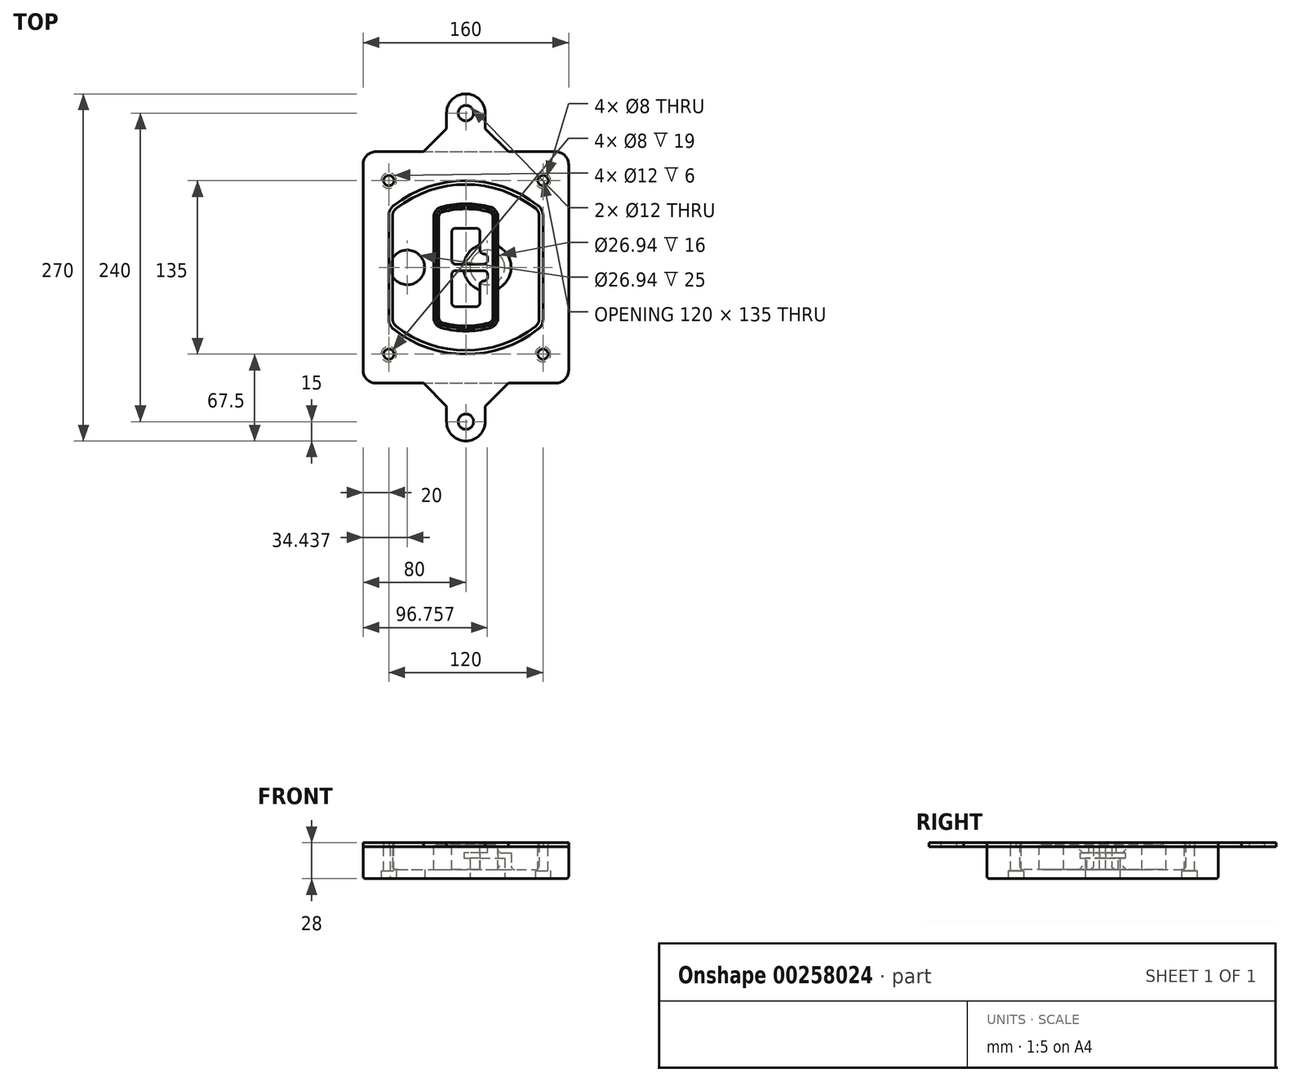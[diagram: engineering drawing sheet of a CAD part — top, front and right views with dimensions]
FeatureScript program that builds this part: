
annotation { "Feature Type Name" : "Feature", "Feature Type Description" : "" }
export const myFeature = defineFeature(function(context is Context, id is Id, definition is map)
    precondition{}
    {
        {
            var Q0;
            Q0=qCreatedBy(makeId("Top.planeOp"),FACE);
            var sketch = newSketch(context, id + "F0", { "sketchPlane" : qUnion([Q0])});
            skPoint(sketch, "E0.rect.middle", {"position": v(0, 0) * mm});
            skLineSegment(sketch, "E1.bottom", {"start": v(-70, -90) * mm, "end": v(70, -90) * mm});
            skLineSegment(sketch, "E1.top", {"start": v(-70, 90) * mm, "end": v(70, 90) * mm});
            skLineSegment(sketch, "E1.left", {"start": v(-80, -80) * mm, "end": v(-80, 80) * mm});
            skLineSegment(sketch, "E1.right", {"start": v(80, -80) * mm, "end": v(80, 80) * mm});
            skLineSegment(sketch, "E2", {"start": v(-80, 90) * mm, "end": v(80, -90) * mm, "construction": true});
            skLineSegment(sketch, "E3", {"start": v(80, 90) * mm, "end": v(-80, -90) * mm, "construction": true});
            skCircle(sketch, "E4", {"center": v(-60, 67.5) * mm, "radius": 4 * mm});
            skCircle(sketch, "E5", {"center": v(60, 67.5) * mm, "radius": 4 * mm});
            skCircle(sketch, "E6", {"center": v(60, -67.5) * mm, "radius": 4 * mm});
            skCircle(sketch, "E7", {"center": v(-60, -67.5) * mm, "radius": 4 * mm});
            skLineSegment(sketch, "E8", {"start": v(-60, 67.5) * mm, "end": v(60, 67.5) * mm, "construction": true});
            skLineSegment(sketch, "E9", {"start": v(60, 67.5) * mm, "end": v(60, -67.5) * mm, "construction": true});
            skLineSegment(sketch, "E10", {"start": v(60, -67.5) * mm, "end": v(-60, -67.5) * mm, "construction": true});
            skLineSegment(sketch, "E11", {"start": v(-60, -67.5) * mm, "end": v(-60, 67.5) * mm, "construction": true});
            skLineSegment(sketch, "E12", {"start": v(-60, 40.3) * mm, "end": v(-60, -40.3) * mm});
            skLineSegment(sketch, "E13", {"start": v(60, 40.3) * mm, "end": v(60, -40.3) * mm});
            skArc(sketch, "E14", {"start": v(56.15, 48.18) * mm, "mid": v(0, 67.5) * mm, "end": v(-56.15, 48.18) * mm});
            skArc(sketch, "E15", {"start": v(-56.15, -48.18) * mm, "mid": v(0, -67.5) * mm, "end": v(56.15, -48.18) * mm});
            skLineSegment(sketch, "E16", {"start": v(-60, 0) * mm, "end": v(60, 0) * mm, "construction": true});
            skPoint(sketch, "E17.visualSharp", {"position": v(-60, -45) * mm});
            skArc(sketch, "E17.filletArc", {"start": v(-60, -40.3) * mm, "mid": v(-58.99, -44.68) * mm, "end": v(-56.15, -48.18) * mm});
            skPoint(sketch, "E18.visualSharp", {"position": v(-60, 45) * mm});
            skArc(sketch, "E18.filletArc", {"start": v(-56.15, 48.18) * mm, "mid": v(-58.99, 44.68) * mm, "end": v(-60, 40.3) * mm});
            skPoint(sketch, "E19.visualSharp", {"position": v(60, 45) * mm});
            skArc(sketch, "E19.filletArc", {"start": v(60, 40.3) * mm, "mid": v(58.99, 44.68) * mm, "end": v(56.15, 48.18) * mm});
            skPoint(sketch, "E20.visualSharp", {"position": v(60, -45) * mm});
            skArc(sketch, "E20.filletArc", {"start": v(56.15, -48.18) * mm, "mid": v(58.99, -44.68) * mm, "end": v(60, -40.3) * mm});
            skPoint(sketch, "E21.visualSharp", {"position": v(-80, 90) * mm});
            skArc(sketch, "E21.filletArc", {"start": v(-70, 90) * mm, "mid": v(-77.07, 87.07) * mm, "end": v(-80, 80) * mm});
            skPoint(sketch, "E22.visualSharp", {"position": v(80, 90) * mm});
            skArc(sketch, "E22.filletArc", {"start": v(80, 80) * mm, "mid": v(77.07, 87.07) * mm, "end": v(70, 90) * mm});
            skPoint(sketch, "E23.visualSharp", {"position": v(80, -90) * mm});
            skArc(sketch, "E23.filletArc", {"start": v(70, -90) * mm, "mid": v(77.07, -87.07) * mm, "end": v(80, -80) * mm});
            skPoint(sketch, "E24.visualSharp", {"position": v(-80, -90) * mm});
            skArc(sketch, "E24.filletArc", {"start": v(-80, -80) * mm, "mid": v(-77.07, -87.07) * mm, "end": v(-70, -90) * mm});
            skArc(sketch, "E25.0", {"start": v(57, 40.3) * mm, "mid": v(56.3, 43.36) * mm, "end": v(54.3, 45.81) * mm});
            skLineSegment(sketch, "E25.1", {"start": v(57, 40.3) * mm, "end": v(57, -40.3) * mm});
            skArc(sketch, "E25.2", {"start": v(54.3, -45.81) * mm, "mid": v(56.3, -43.36) * mm, "end": v(57, -40.3) * mm});
            skArc(sketch, "E25.3", {"start": v(-54.3, -45.81) * mm, "mid": v(0, -64.5) * mm, "end": v(54.3, -45.81) * mm});
            skArc(sketch, "E25.4", {"start": v(-57, -40.3) * mm, "mid": v(-56.3, -43.36) * mm, "end": v(-54.3, -45.81) * mm});
            skArc(sketch, "E25.5", {"start": v(54.3, 45.81) * mm, "mid": v(0, 64.5) * mm, "end": v(-54.3, 45.81) * mm});
            skLineSegment(sketch, "E25.6", {"start": v(-57, 40.3) * mm, "end": v(-57, -40.3) * mm});
            skArc(sketch, "E25.7", {"start": v(-54.3, 45.81) * mm, "mid": v(-56.3, 43.36) * mm, "end": v(-57, 40.3) * mm});
            skArc(sketch, "E26.0", {"start": v(-58.62, 51.33) * mm, "mid": v(-62.58, 46.43) * mm, "end": v(-64, 40.3) * mm});
            skArc(sketch, "E26.1", {"start": v(58.62, 51.33) * mm, "mid": v(0, 71.5) * mm, "end": v(-58.62, 51.33) * mm});
            skArc(sketch, "E26.2", {"start": v(64, 40.3) * mm, "mid": v(62.58, 46.43) * mm, "end": v(58.62, 51.33) * mm});
            skLineSegment(sketch, "E26.3", {"start": v(64, 40.3) * mm, "end": v(64, -40.3) * mm});
            skArc(sketch, "E26.4", {"start": v(58.62, -51.33) * mm, "mid": v(62.58, -46.43) * mm, "end": v(64, -40.3) * mm});
            skLineSegment(sketch, "E26.5", {"start": v(-64, 40.3) * mm, "end": v(-64, -40.3) * mm});
            skArc(sketch, "E26.6", {"start": v(-58.62, -51.33) * mm, "mid": v(0, -71.5) * mm, "end": v(58.62, -51.33) * mm});
            skArc(sketch, "E26.7", {"start": v(-64, -40.3) * mm, "mid": v(-62.58, -46.43) * mm, "end": v(-58.62, -51.33) * mm});
            skSolve(sketch);
        }
        {
            var Q0;
            Q0=makeQuery(id+"F0.imprint","IMPRINT",FACE,{"disambiguationData":[TD([[makeQuery(id+"F0.imprint","IMPRINT",EDGE,{"derivedFrom":sQuery(id+"F0.wireOp",EDGE,"E1.bottom")}),1.0]])]});
            var Q1;
            Q1=makeQuery(id+"F0.imprint","IMPRINT",FACE,{"disambiguationData":[TD([[makeQuery(id+"F0.imprint","IMPRINT",EDGE,{"derivedFrom":sQuery(id+"F0.wireOp",EDGE,"E12")}),1.0]])]});
            var Q2;
            Q2=makeQuery(id+"F0.imprint","IMPRINT",FACE,{"disambiguationData":[TD([[makeQuery(id+"F0.imprint","IMPRINT",EDGE,{"derivedFrom":sQuery(id+"F0.wireOp",EDGE,"E25.0")}),1.0]])]});
            var Q3;
            Q3=makeQuery(id+"F0.imprint","IMPRINT",FACE,{"disambiguationData":[TD([[makeQuery(id+"F0.imprint","IMPRINT",EDGE,{"derivedFrom":sQuery(id+"F0.wireOp",EDGE,"E12")}),-1.0]])]});
            extrude(context, id + "F1", {"entities" : qUnion([Q0, Q1, Q2, Q3]), "oppositeDirection" : true, "depth" : 25 * mm});
        }
        {
            var Q0;
            Q0=makeQuery(id+"F0.imprint","IMPRINT",FACE,{"disambiguationData":[TD([[makeQuery(id+"F0.imprint","IMPRINT",EDGE,{"derivedFrom":sQuery(id+"F0.wireOp",EDGE,"E12")}),1.0]])]});
            extrude(context, id + "F2", {"entities" : qUnion([Q0]), "operationType" : NewBodyOperationType.ADD, "depth" : 3 * mm});
        }
        {
            var Q0;
            Q0=makeQuery(id+"F0.imprint","IMPRINT",FACE,{"disambiguationData":[TD([[makeQuery(id+"F0.imprint","IMPRINT",EDGE,{"derivedFrom":sQuery(id+"F0.wireOp",EDGE,"E25.0")}),1.0]])]});
            extrude(context, id + "F3", {"entities" : qUnion([Q0]), "operationType" : NewBodyOperationType.REMOVE, "oppositeDirection" : true, "depth" : 18 * mm});
        }
        {
            var Q0;
            Q0=makeQuery(id+"F2.opExtrude","CAP_FACE",FACE,{"disambiguationData":[OSD([sQuery(id+"F0.wireOp",EDGE,"E12"),sQuery(id+"F0.wireOp",EDGE,"E13"),sQuery(id+"F0.wireOp",EDGE,"E14"),sQuery(id+"F0.wireOp",EDGE,"E15"),sQuery(id+"F0.wireOp",EDGE,"E17.filletArc"),sQuery(id+"F0.wireOp",EDGE,"E18.filletArc"),sQuery(id+"F0.wireOp",EDGE,"E19.filletArc"),sQuery(id+"F0.wireOp",EDGE,"E20.filletArc"),sQuery(id+"F0.wireOp",EDGE,"E25.0"),sQuery(id+"F0.wireOp",EDGE,"E25.1"),sQuery(id+"F0.wireOp",EDGE,"E25.2"),sQuery(id+"F0.wireOp",EDGE,"E25.3"),sQuery(id+"F0.wireOp",EDGE,"E25.4"),sQuery(id+"F0.wireOp",EDGE,"E25.5"),sQuery(id+"F0.wireOp",EDGE,"E25.6"),sQuery(id+"F0.wireOp",EDGE,"E25.7")])],"isStart":false});
            var sketch = newSketch(context, id + "F4", { "sketchPlane" : qUnion([Q0])});
            skArc(sketch, "E27.0", {"start": v(-19.08, -46.97) * mm, "mid": v(0, -49.5) * mm, "end": v(19.08, -46.97) * mm});
            skArc(sketch, "E28.0", {"start": v(19.08, 46.97) * mm, "mid": v(0, 49.5) * mm, "end": v(-19.08, 46.97) * mm});
            skLineSegment(sketch, "E29", {"start": v(-25, 39.25) * mm, "end": v(-25, -39.25) * mm});
            skLineSegment(sketch, "E30", {"start": v(25, 39.25) * mm, "end": v(25, -39.25) * mm});
            skLineSegment(sketch, "E31", {"start": v(-25, 45.1) * mm, "end": v(25, 45.1) * mm, "construction": true});
            skLineSegment(sketch, "E32", {"start": v(-25, -45.1) * mm, "end": v(25, -45.1) * mm, "construction": true});
            skPoint(sketch, "E33.visualSharp", {"position": v(-25, 45.1) * mm});
            skArc(sketch, "E33.filletArc", {"start": v(-19.08, 46.97) * mm, "mid": v(-23.35, 44.11) * mm, "end": v(-25, 39.25) * mm});
            skPoint(sketch, "E34.visualSharp", {"position": v(25, 45.1) * mm});
            skArc(sketch, "E34.filletArc", {"start": v(25, 39.25) * mm, "mid": v(23.35, 44.11) * mm, "end": v(19.08, 46.97) * mm});
            skPoint(sketch, "E35.visualSharp", {"position": v(25, -45.1) * mm});
            skArc(sketch, "E35.filletArc", {"start": v(19.08, -46.97) * mm, "mid": v(23.35, -44.11) * mm, "end": v(25, -39.25) * mm});
            skPoint(sketch, "E36.visualSharp", {"position": v(-25, -45.1) * mm});
            skArc(sketch, "E36.filletArc", {"start": v(-25, -39.25) * mm, "mid": v(-23.35, -44.11) * mm, "end": v(-19.08, -46.97) * mm});
            skArc(sketch, "E37.0", {"start": v(54.3, 45.81) * mm, "mid": v(0, 64.5) * mm, "end": v(-54.3, 45.81) * mm});
            skArc(sketch, "E37.1", {"start": v(-54.3, 45.81) * mm, "mid": v(-56.3, 43.36) * mm, "end": v(-57, 40.3) * mm});
            skLineSegment(sketch, "E37.2", {"start": v(-57, 40.3) * mm, "end": v(-57, -40.3) * mm});
            skArc(sketch, "E37.3", {"start": v(-57, -40.3) * mm, "mid": v(-56.3, -43.36) * mm, "end": v(-54.3, -45.81) * mm});
            skArc(sketch, "E37.4", {"start": v(-54.3, -45.81) * mm, "mid": v(0, -64.5) * mm, "end": v(54.3, -45.81) * mm});
            skArc(sketch, "E37.5", {"start": v(54.3, -45.81) * mm, "mid": v(56.3, -43.36) * mm, "end": v(57, -40.3) * mm});
            skLineSegment(sketch, "E37.6", {"start": v(57, 40.3) * mm, "end": v(57, -40.3) * mm});
            skArc(sketch, "E37.7", {"start": v(57, 40.3) * mm, "mid": v(56.3, 43.36) * mm, "end": v(54.3, 45.81) * mm});
            skLineSegment(sketch, "E38.0", {"start": v(23, 39.25) * mm, "end": v(23, -39.25) * mm});
            skArc(sketch, "E38.1", {"start": v(18.56, -45.04) * mm, "mid": v(21.76, -42.9) * mm, "end": v(23, -39.25) * mm});
            skArc(sketch, "E38.2", {"start": v(-18.56, -45.04) * mm, "mid": v(0, -47.5) * mm, "end": v(18.56, -45.04) * mm});
            skArc(sketch, "E38.3", {"start": v(-23, -39.25) * mm, "mid": v(-21.76, -42.9) * mm, "end": v(-18.56, -45.04) * mm});
            skLineSegment(sketch, "E38.4", {"start": v(-23, 39.25) * mm, "end": v(-23, -39.25) * mm});
            skArc(sketch, "E38.5", {"start": v(23, 39.25) * mm, "mid": v(21.76, 42.9) * mm, "end": v(18.56, 45.04) * mm});
            skArc(sketch, "E38.6", {"start": v(-18.56, 45.04) * mm, "mid": v(-21.76, 42.9) * mm, "end": v(-23, 39.25) * mm});
            skArc(sketch, "E38.7", {"start": v(18.56, 45.04) * mm, "mid": v(0, 47.5) * mm, "end": v(-18.56, 45.04) * mm});
            skArc(sketch, "E39.0", {"start": v(21, 39.25) * mm, "mid": v(20.18, 41.68) * mm, "end": v(18.04, 43.1) * mm});
            skLineSegment(sketch, "E39.1", {"start": v(21, 39.25) * mm, "end": v(21, -39.25) * mm});
            skArc(sketch, "E39.2", {"start": v(18.04, -43.1) * mm, "mid": v(20.18, -41.68) * mm, "end": v(21, -39.25) * mm});
            skArc(sketch, "E39.3", {"start": v(-18.04, -43.1) * mm, "mid": v(0, -45.5) * mm, "end": v(18.04, -43.1) * mm});
            skArc(sketch, "E39.4", {"start": v(-21, -39.25) * mm, "mid": v(-20.18, -41.68) * mm, "end": v(-18.04, -43.1) * mm});
            skArc(sketch, "E39.5", {"start": v(18.04, 43.1) * mm, "mid": v(0, 45.5) * mm, "end": v(-18.04, 43.1) * mm});
            skLineSegment(sketch, "E39.6", {"start": v(-21, 39.25) * mm, "end": v(-21, -39.25) * mm});
            skArc(sketch, "E39.7", {"start": v(-18.04, 43.1) * mm, "mid": v(-20.18, 41.68) * mm, "end": v(-21, 39.25) * mm});
            skLineSegment(sketch, "E40", {"start": v(-25, 0) * mm, "end": v(25, 0) * mm, "construction": true});
            skLineSegment(sketch, "E41", {"start": v(-11, 5.5) * mm, "end": v(-11, 27.5) * mm});
            skLineSegment(sketch, "E42", {"start": v(-8, 30.5) * mm, "end": v(8, 30.5) * mm});
            skLineSegment(sketch, "E43", {"start": v(11, 27.5) * mm, "end": v(11, 13.5) * mm});
            skLineSegment(sketch, "E44", {"start": v(14, 10.5) * mm, "end": v(14, 10.5) * mm});
            skLineSegment(sketch, "E45", {"start": v(17, 7.5) * mm, "end": v(17, 5.5) * mm});
            skLineSegment(sketch, "E46", {"start": v(14, 2.5) * mm, "end": v(-8, 2.5) * mm});
            skPoint(sketch, "E47.visualSharp", {"position": v(-11, 30.5) * mm});
            skArc(sketch, "E47.filletArc", {"start": v(-8, 30.5) * mm, "mid": v(-10.12, 29.62) * mm, "end": v(-11, 27.5) * mm});
            skPoint(sketch, "E48.visualSharp", {"position": v(11, 30.5) * mm});
            skArc(sketch, "E48.filletArc", {"start": v(11, 27.5) * mm, "mid": v(10.12, 29.62) * mm, "end": v(8, 30.5) * mm});
            skPoint(sketch, "E49.visualSharp", {"position": v(11, 10.5) * mm});
            skArc(sketch, "E49.filletArc", {"start": v(11, 13.5) * mm, "mid": v(11.88, 11.38) * mm, "end": v(14, 10.5) * mm});
            skPoint(sketch, "E50.visualSharp", {"position": v(17, 10.5) * mm});
            skArc(sketch, "E50.filletArc", {"start": v(17, 7.5) * mm, "mid": v(16.12, 9.62) * mm, "end": v(14, 10.5) * mm});
            skPoint(sketch, "E51.visualSharp", {"position": v(17, 2.5) * mm});
            skArc(sketch, "E51.filletArc", {"start": v(14, 2.5) * mm, "mid": v(16.12, 3.38) * mm, "end": v(17, 5.5) * mm});
            skPoint(sketch, "E52.visualSharp", {"position": v(-11, 2.5) * mm});
            skArc(sketch, "E52.filletArc", {"start": v(-11, 5.5) * mm, "mid": v(-10.12, 3.38) * mm, "end": v(-8, 2.5) * mm});
            skLineSegment(sketch, "E53.0.MirrorCS", {"start": v(14, -2.5) * mm, "end": v(-8, -2.5) * mm});
            skArc(sketch, "E54.0.MirrorCS", {"start": v(-11, -5.5) * mm, "mid": v(-10.12, -3.38) * mm, "end": v(-8, -2.5) * mm});
            skLineSegment(sketch, "E55.0.MirrorCS", {"start": v(-11, -5.5) * mm, "end": v(-11, -27.5) * mm});
            skArc(sketch, "E56.0.MirrorCS", {"start": v(-8, -30.5) * mm, "mid": v(-10.12, -29.62) * mm, "end": v(-11, -27.5) * mm});
            skLineSegment(sketch, "E57.0.MirrorCS", {"start": v(-8, -30.5) * mm, "end": v(8, -30.5) * mm});
            skArc(sketch, "E58.0.MirrorCS", {"start": v(11, -27.5) * mm, "mid": v(10.12, -29.62) * mm, "end": v(8, -30.5) * mm});
            skLineSegment(sketch, "E59.0.MirrorCS", {"start": v(11, -27.5) * mm, "end": v(11, -13.5) * mm});
            skArc(sketch, "E60.0.MirrorCS", {"start": v(11, -13.5) * mm, "mid": v(11.88, -11.38) * mm, "end": v(14, -10.5) * mm});
            skArc(sketch, "E61.0.MirrorCS", {"start": v(17, -7.5) * mm, "mid": v(16.12, -9.62) * mm, "end": v(14, -10.5) * mm});
            skLineSegment(sketch, "E62.0.MirrorCS", {"start": v(17, -7.5) * mm, "end": v(17, -5.5) * mm});
            skArc(sketch, "E63.0.MirrorCS", {"start": v(14, -2.5) * mm, "mid": v(16.12, -3.38) * mm, "end": v(17, -5.5) * mm});
            skSolve(sketch);
        }
        {
            var Q0;
            Q0=makeQuery(id+"F4.imprint","IMPRINT",FACE,{"disambiguationData":[TD([[makeQuery(id+"F4.imprint","IMPRINT",EDGE,{"derivedFrom":sQuery(id+"F4.wireOp",EDGE,"E27.0")}),1.0]])]});
            var Q1;
            Q1=makeQuery(id+"F4.imprint","IMPRINT",FACE,{"disambiguationData":[TD([[makeQuery(id+"F4.imprint","IMPRINT",EDGE,{"derivedFrom":sQuery(id+"F4.wireOp",EDGE,"E38.0")}),-1.0]])]});
            var Q2;
            Q2=makeQuery(id+"F4.imprint","IMPRINT",FACE,{"disambiguationData":[TD([[makeQuery(id+"F4.imprint","IMPRINT",EDGE,{"derivedFrom":sQuery(id+"F4.wireOp",EDGE,"E39.0")}),1.0]])]});
            extrude(context, id + "F5", {"entities" : qUnion([Q0, Q1, Q2]), "operationType" : NewBodyOperationType.ADD, "endBound" : BoundingType.UP_TO_NEXT, "oppositeDirection" : true, "depth" : 25 * mm});
        }
        {
            var Q0;
            Q0=makeQuery(id+"F4.imprint","IMPRINT",FACE,{"disambiguationData":[TD([[makeQuery(id+"F4.imprint","IMPRINT",EDGE,{"derivedFrom":sQuery(id+"F4.wireOp",EDGE,"E38.0")}),-1.0]])]});
            extrude(context, id + "F6", {"entities" : qUnion([Q0]), "operationType" : NewBodyOperationType.REMOVE, "oppositeDirection" : true, "depth" : 2 * mm});
        }
        {
            var Q0;
            Q0=makeQuery(id+"F1.opExtrude","CAP_FACE",FACE,{"disambiguationData":[OSD([sQuery(id+"F0.wireOp",EDGE,"E1.bottom"),sQuery(id+"F0.wireOp",EDGE,"E1.top"),sQuery(id+"F0.wireOp",EDGE,"E1.left"),sQuery(id+"F0.wireOp",EDGE,"E1.right"),sQuery(id+"F0.wireOp",EDGE,"E4"),sQuery(id+"F0.wireOp",EDGE,"E5"),sQuery(id+"F0.wireOp",EDGE,"E6"),sQuery(id+"F0.wireOp",EDGE,"E7"),sQuery(id+"F0.wireOp",EDGE,"E21.filletArc"),sQuery(id+"F0.wireOp",EDGE,"E22.filletArc"),sQuery(id+"F0.wireOp",EDGE,"E23.filletArc"),sQuery(id+"F0.wireOp",EDGE,"E24.filletArc")])],"isStart":false});
            var sketch = newSketch(context, id + "F7", { "sketchPlane" : qUnion([Q0])});
            skCircle(sketch, "E64", {"center": v(16.76, 0) * mm, "radius": 13.47 * mm});
            skCircle(sketch, "E65", {"center": v(-45.56, 0) * mm, "radius": 13.47 * mm});
            skLineSegment(sketch, "E66", {"start": v(80, 0) * mm, "end": v(-80, 0) * mm});
            skCircle(sketch, "E67", {"center": v(16.76, 0) * mm, "radius": 18.47 * mm});
            skCircle(sketch, "E68", {"center": v(60, -67.5) * mm, "radius": 6 * mm});
            skCircle(sketch, "E69", {"center": v(-60, -67.5) * mm, "radius": 6 * mm});
            skCircle(sketch, "E70", {"center": v(-60, 67.5) * mm, "radius": 6 * mm});
            skCircle(sketch, "E71", {"center": v(60, 67.5) * mm, "radius": 6 * mm});
            skSolve(sketch);
        }
        {
            var Q0;
            {var subQ1=sQuery(id+"F7.wireOp",EDGE,"E66");var subQ4=sQuery(id+"F7.wireOp",EDGE,"E64");var subQ6=makeQuery(id+"F7.imprint","INTERSECT",VERTEX,{"disambiguationData":[OD(0.0)],"derivedFrom":[subQ4,subQ1]});Q0=makeQuery(id+"F7.imprint","IMPRINT",FACE,{"disambiguationData":[TD([[makeQuery(id+"F7.imprint","IMPRINT",EDGE,{"disambiguationData":[TD([[subQ6,-1.0]])],"derivedFrom":subQ4}),-1.0]])]});}
            var Q1;
            {var subQ0=sQuery(id+"F7.wireOp",EDGE,"E66");var subQ1=sQuery(id+"F7.wireOp",EDGE,"E64");var subQ3=makeQuery(id+"F7.imprint","INTERSECT",VERTEX,{"disambiguationData":[OD(0.0)],"derivedFrom":[subQ1,subQ0]});Q1=makeQuery(id+"F7.imprint","IMPRINT",FACE,{"disambiguationData":[TD([[makeQuery(id+"F7.imprint","IMPRINT",EDGE,{"disambiguationData":[TD([[subQ3,-1.0]])],"derivedFrom":subQ1}),1.0]])]});}
            var Q2;
            {var subQ0=sQuery(id+"F7.wireOp",EDGE,"E66");var subQ1=sQuery(id+"F7.wireOp",EDGE,"E64");var subQ3=makeQuery(id+"F7.imprint","INTERSECT",VERTEX,{"disambiguationData":[OD(0.0)],"derivedFrom":[subQ1,subQ0]});Q2=makeQuery(id+"F7.imprint","IMPRINT",FACE,{"disambiguationData":[TD([[makeQuery(id+"F7.imprint","IMPRINT",EDGE,{"disambiguationData":[TD([[subQ3,1.0]])],"derivedFrom":subQ1}),1.0]])]});}
            var Q3;
            {var subQ1=sQuery(id+"F7.wireOp",EDGE,"E66");var subQ4=sQuery(id+"F7.wireOp",EDGE,"E64");var subQ6=makeQuery(id+"F7.imprint","INTERSECT",VERTEX,{"disambiguationData":[OD(0.0)],"derivedFrom":[subQ4,subQ1]});Q3=makeQuery(id+"F7.imprint","IMPRINT",FACE,{"disambiguationData":[TD([[makeQuery(id+"F7.imprint","IMPRINT",EDGE,{"disambiguationData":[TD([[subQ6,1.0]])],"derivedFrom":subQ4}),-1.0]])]});}
            extrude(context, id + "F8", {"entities" : qUnion([Q0, Q1, Q2, Q3]), "operationType" : NewBodyOperationType.ADD, "oppositeDirection" : true, "depth" : 20 * mm});
        }
        {
            var Q0;
            {var subQ0=sQuery(id+"F7.wireOp",EDGE,"E66");var subQ1=sQuery(id+"F7.wireOp",EDGE,"E64");var subQ3=makeQuery(id+"F7.imprint","INTERSECT",VERTEX,{"disambiguationData":[OD(0.0)],"derivedFrom":[subQ1,subQ0]});Q0=makeQuery(id+"F7.imprint","IMPRINT",FACE,{"disambiguationData":[TD([[makeQuery(id+"F7.imprint","IMPRINT",EDGE,{"disambiguationData":[TD([[subQ3,-1.0]])],"derivedFrom":subQ1}),1.0]])]});}
            var Q1;
            {var subQ0=sQuery(id+"F7.wireOp",EDGE,"E66");var subQ1=sQuery(id+"F7.wireOp",EDGE,"E64");var subQ3=makeQuery(id+"F7.imprint","INTERSECT",VERTEX,{"disambiguationData":[OD(0.0)],"derivedFrom":[subQ1,subQ0]});Q1=makeQuery(id+"F7.imprint","IMPRINT",FACE,{"disambiguationData":[TD([[makeQuery(id+"F7.imprint","IMPRINT",EDGE,{"disambiguationData":[TD([[subQ3,1.0]])],"derivedFrom":subQ1}),1.0]])]});}
            extrude(context, id + "F9", {"entities" : qUnion([Q0, Q1]), "operationType" : NewBodyOperationType.REMOVE, "oppositeDirection" : true, "depth" : 16 * mm});
        }
        {
            var Q0;
            {var subQ0=sQuery(id+"F7.wireOp",EDGE,"E66");var subQ1=sQuery(id+"F7.wireOp",EDGE,"E65");var subQ3=makeQuery(id+"F7.imprint","INTERSECT",VERTEX,{"disambiguationData":[OD(0.0)],"derivedFrom":[subQ1,subQ0]});Q0=makeQuery(id+"F7.imprint","IMPRINT",FACE,{"disambiguationData":[TD([[makeQuery(id+"F7.imprint","IMPRINT",EDGE,{"disambiguationData":[TD([[subQ3,-1.0]])],"derivedFrom":subQ1}),1.0]])]});}
            var Q1;
            {var subQ0=sQuery(id+"F7.wireOp",EDGE,"E66");var subQ1=sQuery(id+"F7.wireOp",EDGE,"E65");var subQ3=makeQuery(id+"F7.imprint","INTERSECT",VERTEX,{"disambiguationData":[OD(0.0)],"derivedFrom":[subQ1,subQ0]});Q1=makeQuery(id+"F7.imprint","IMPRINT",FACE,{"disambiguationData":[TD([[makeQuery(id+"F7.imprint","IMPRINT",EDGE,{"disambiguationData":[TD([[subQ3,1.0]])],"derivedFrom":subQ1}),1.0]])]});}
            extrude(context, id + "F10", {"entities" : qUnion([Q0, Q1]), "operationType" : NewBodyOperationType.REMOVE, "oppositeDirection" : true, "depth" : 25 * mm});
        }
        {
            var Q0;
            Q0=makeQuery(id+"F7.imprint","IMPRINT",FACE,{"disambiguationData":[TD([[makeQuery(id+"F7.imprint","IMPRINT",EDGE,{"derivedFrom":sQuery(id+"F7.wireOp",EDGE,"E68")}),1.0]])]});
            var Q1;
            Q1=makeQuery(id+"F7.imprint","IMPRINT",FACE,{"disambiguationData":[TD([[makeQuery(id+"F7.imprint","IMPRINT",EDGE,{"derivedFrom":makeQuery(id+"F1.opExtrude","CAP_EDGE",EDGE,{"disambiguationData":[OSD([sQuery(id+"F0.wireOp",EDGE,"E5")])],"isStart":false})}),-1.0]])]});
            var Q2;
            Q2=makeQuery(id+"F7.imprint","IMPRINT",FACE,{"disambiguationData":[TD([[makeQuery(id+"F7.imprint","IMPRINT",EDGE,{"derivedFrom":sQuery(id+"F7.wireOp",EDGE,"E69")}),1.0]])]});
            var Q3;
            Q3=makeQuery(id+"F7.imprint","IMPRINT",FACE,{"disambiguationData":[TD([[makeQuery(id+"F7.imprint","IMPRINT",EDGE,{"derivedFrom":makeQuery(id+"F1.opExtrude","CAP_EDGE",EDGE,{"disambiguationData":[OSD([sQuery(id+"F0.wireOp",EDGE,"E4")])],"isStart":false})}),-1.0]])]});
            var Q4;
            Q4=makeQuery(id+"F7.imprint","IMPRINT",FACE,{"disambiguationData":[TD([[makeQuery(id+"F7.imprint","IMPRINT",EDGE,{"derivedFrom":sQuery(id+"F7.wireOp",EDGE,"E70")}),1.0]])]});
            var Q5;
            Q5=makeQuery(id+"F7.imprint","IMPRINT",FACE,{"disambiguationData":[TD([[makeQuery(id+"F7.imprint","IMPRINT",EDGE,{"derivedFrom":makeQuery(id+"F1.opExtrude","CAP_EDGE",EDGE,{"disambiguationData":[OSD([sQuery(id+"F0.wireOp",EDGE,"E7")])],"isStart":false})}),-1.0]])]});
            var Q6;
            Q6=makeQuery(id+"F7.imprint","IMPRINT",FACE,{"disambiguationData":[TD([[makeQuery(id+"F7.imprint","IMPRINT",EDGE,{"derivedFrom":sQuery(id+"F7.wireOp",EDGE,"E71")}),1.0]])]});
            var Q7;
            Q7=makeQuery(id+"F7.imprint","IMPRINT",FACE,{"disambiguationData":[TD([[makeQuery(id+"F7.imprint","IMPRINT",EDGE,{"derivedFrom":makeQuery(id+"F1.opExtrude","CAP_EDGE",EDGE,{"disambiguationData":[OSD([sQuery(id+"F0.wireOp",EDGE,"E6")])],"isStart":false})}),-1.0]])]});
            extrude(context, id + "F11", {"entities" : qUnion([Q0, Q1, Q2, Q3, Q4, Q5, Q6, Q7]), "operationType" : NewBodyOperationType.REMOVE, "oppositeDirection" : true, "depth" : 6 * mm});
        }
        {
            var Q0;
            Q0=makeQuery(id+"F9.boolean.opBoolean","COPY",FACE,{"derivedFrom":makeQuery(id+"F9.opExtrude","CAP_FACE",FACE,{"disambiguationData":[OSD([sQuery(id+"F7.wireOp",EDGE,"E64")])],"isStart":false})});
            var sketch = newSketch(context, id + "F12", { "sketchPlane" : qUnion([Q0])});
            skArc(sketch, "E72.0", {"start": v(11, 17.55) * mm, "mid": v(2.57, 11.82) * mm, "end": v(-1.54, 2.5) * mm});
            skArc(sketch, "E72.1", {"start": v(-1.54, -2.5) * mm, "mid": v(2.57, -11.82) * mm, "end": v(11, -17.55) * mm});
            skLineSegment(sketch, "E73", {"start": v(-1.54, -2.5) * mm, "end": v(14, -2.5) * mm});
            skLineSegment(sketch, "E74.0", {"start": v(14, 2.5) * mm, "end": v(-1.54, 2.5) * mm});
            skArc(sketch, "E74.1", {"start": v(14, 2.5) * mm, "mid": v(16.12, 3.38) * mm, "end": v(17, 5.5) * mm});
            skLineSegment(sketch, "E74.2", {"start": v(17, 7.5) * mm, "end": v(17, 5.5) * mm});
            skArc(sketch, "E74.3", {"start": v(17, 7.5) * mm, "mid": v(16.12, 9.62) * mm, "end": v(14, 10.5) * mm});
            skArc(sketch, "E74.4", {"start": v(11, 13.5) * mm, "mid": v(11.88, 11.38) * mm, "end": v(14, 10.5) * mm});
            skLineSegment(sketch, "E74.5", {"start": v(11, 17.55) * mm, "end": v(11, 13.5) * mm});
            skLineSegment(sketch, "E74.7", {"start": v(14, -2.5) * mm, "end": v(-1.54, -2.5) * mm});
            skArc(sketch, "E74.8", {"start": v(14, -2.5) * mm, "mid": v(16.12, -3.38) * mm, "end": v(17, -5.5) * mm});
            skLineSegment(sketch, "E74.9", {"start": v(17, -7.5) * mm, "end": v(17, -5.5) * mm});
            skArc(sketch, "E74.10", {"start": v(17, -7.5) * mm, "mid": v(16.12, -9.62) * mm, "end": v(14, -10.5) * mm});
            skArc(sketch, "E74.11", {"start": v(11, -13.5) * mm, "mid": v(11.88, -11.38) * mm, "end": v(14, -10.5) * mm});
            skLineSegment(sketch, "E74.12", {"start": v(11, -17.55) * mm, "end": v(11, -13.5) * mm});
            skPoint(sketch, "E75.orphan", {"position": v(11, -27.5) * mm});
            skPoint(sketch, "E76.orphan", {"position": v(-8, -2.5) * mm});
            skPoint(sketch, "E77.orphan", {"position": v(-8, 2.5) * mm});
            skPoint(sketch, "E78.orphan", {"position": v(11, 27.5) * mm});
            skSolve(sketch);
        }
        {
            var Q0;
            {var subQ7=sQuery(id+"F12.wireOp",EDGE,"E72.0");var subQ14=sQuery(id+"F12.wireOp",EDGE,"E72.1");var subQ16=sQuery(id+"F12.wireOp",EDGE,"E74.1");var subQ18=sQuery(id+"F12.wireOp",EDGE,"E74.8");Q0=qUnion([makeQuery(id+"F12.imprint","IMPRINT",FACE,{"disambiguationData":[TD([[makeQuery(id+"F12.imprint","IMPRINT",EDGE,{"derivedFrom":subQ7}),1.0]])]}),makeQuery(id+"F12.imprint","IMPRINT",FACE,{"disambiguationData":[TD([[makeQuery(id+"F12.imprint","IMPRINT",EDGE,{"derivedFrom":subQ14}),1.0]])]}),makeQuery(id+"F12.imprint","IMPRINT",FACE,{"disambiguationData":[TD([[makeQuery(id+"F12.imprint","IMPRINT",EDGE,{"derivedFrom":subQ16}),1.0]])]}),makeQuery(id+"F12.imprint","IMPRINT",FACE,{"disambiguationData":[TD([[makeQuery(id+"F12.imprint","IMPRINT",EDGE,{"derivedFrom":subQ18}),-1.0]])]})]);}
            var Q1;
            Q1=makeQuery(id+"F5.boolean.opBoolean","SPLIT",FACE,{"disambiguationData":[TD([makeQuery(id+"F5.opExtrude","SWEPT_FACE",FACE,{"disambiguationData":[OSD([sQuery(id+"F4.wireOp",EDGE,"E41")])]})])],"derivedFrom":makeQuery(id+"F3.boolean.opBoolean","COPY",FACE,{"derivedFrom":makeQuery(id+"F3.opExtrude","CAP_FACE",FACE,{"disambiguationData":[OSD([sQuery(id+"F0.wireOp",EDGE,"E25.0"),sQuery(id+"F0.wireOp",EDGE,"E25.1"),sQuery(id+"F0.wireOp",EDGE,"E25.2"),sQuery(id+"F0.wireOp",EDGE,"E25.3"),sQuery(id+"F0.wireOp",EDGE,"E25.4"),sQuery(id+"F0.wireOp",EDGE,"E25.5"),sQuery(id+"F0.wireOp",EDGE,"E25.6"),sQuery(id+"F0.wireOp",EDGE,"E25.7")])],"isStart":false})})});
            extrude(context, id + "F13", {"entities" : qUnion([Q0]), "operationType" : NewBodyOperationType.REMOVE, "endBound" : BoundingType.UP_TO_SURFACE, "endBoundEntityFace" : qUnion([Q1]), "depth" : 25 * mm});
        }
        {
            var Q0;
            Q0=makeQuery(id+"F3.boolean.opBoolean","COPY",EDGE,{"derivedFrom":makeQuery(id+"F3.opExtrude","CAP_EDGE",EDGE,{"disambiguationData":[OSD([sQuery(id+"F0.wireOp",EDGE,"E25.6")])],"isStart":false})});
            var Q1;
            Q1=makeQuery(id+"F8.boolean.opBoolean","INTERSECT",EDGE,{"derivedFrom":[makeQuery(id+"F5.opExtrude","SWEPT_FACE",FACE,{"disambiguationData":[OSD([sQuery(id+"F4.wireOp",EDGE,"E30")])]}),makeQuery(id+"F8.opExtrude","CAP_FACE",FACE,{"disambiguationData":[OSD([sQuery(id+"F7.wireOp",EDGE,"E67")])],"isStart":false})]});
            var Q2;
            Q2=makeQuery(id+"F8.boolean.opBoolean","INTERSECT",EDGE,{"disambiguationData":[OD(1.0)],"derivedFrom":[makeQuery(id+"F5.opExtrude","SWEPT_FACE",FACE,{"disambiguationData":[OSD([sQuery(id+"F4.wireOp",EDGE,"E30")])]}),makeQuery(id+"F8.opExtrude","SWEPT_FACE",FACE,{"disambiguationData":[OSD([sQuery(id+"F7.wireOp",EDGE,"E67")])]})]});
            var Q3;
            {var subQ0=makeQuery(id+"F3.boolean.opBoolean","COPY",FACE,{"derivedFrom":makeQuery(id+"F3.opExtrude","CAP_FACE",FACE,{"disambiguationData":[OSD([sQuery(id+"F0.wireOp",EDGE,"E25.0"),sQuery(id+"F0.wireOp",EDGE,"E25.1"),sQuery(id+"F0.wireOp",EDGE,"E25.2"),sQuery(id+"F0.wireOp",EDGE,"E25.3"),sQuery(id+"F0.wireOp",EDGE,"E25.4"),sQuery(id+"F0.wireOp",EDGE,"E25.5"),sQuery(id+"F0.wireOp",EDGE,"E25.6"),sQuery(id+"F0.wireOp",EDGE,"E25.7")])],"isStart":false})});var subQ1=sQuery(id+"F4.wireOp",EDGE,"E30");Q3=makeQuery(id+"F8.boolean.opBoolean","SPLIT",EDGE,{"disambiguationData":[TD([makeQuery(id+"F5.opExtrude","SWEPT_FACE",FACE,{"disambiguationData":[OSD([sQuery(id+"F4.wireOp",EDGE,"E35.filletArc")])]})])],"derivedFrom":makeQuery(id+"F5.opExtrude","TWEAK_EDGE",EDGE,{"derivedFrom":[subQ0,makeQuery(id+"F4.imprint","IMPRINT",EDGE,{"derivedFrom":subQ1})]})});}
            var Q4;
            {var subQ0=sQuery(id+"F0.wireOp",EDGE,"E25.0");var subQ1=sQuery(id+"F0.wireOp",EDGE,"E25.1");var subQ2=sQuery(id+"F0.wireOp",EDGE,"E25.2");var subQ3=sQuery(id+"F0.wireOp",EDGE,"E25.3");var subQ4=sQuery(id+"F0.wireOp",EDGE,"E25.4");var subQ5=sQuery(id+"F0.wireOp",EDGE,"E25.5");var subQ6=sQuery(id+"F0.wireOp",EDGE,"E25.6");var subQ7=sQuery(id+"F0.wireOp",EDGE,"E25.7");Q4=makeQuery(id+"F8.boolean.opBoolean","INTERSECT",EDGE,{"derivedFrom":[makeQuery(id+"F5.boolean.opBoolean","SPLIT",FACE,{"disambiguationData":[TD([makeQuery(id+"F2.opExtrude","SWEPT_FACE",FACE,{"disambiguationData":[OSD([subQ0])]})])],"derivedFrom":makeQuery(id+"F3.boolean.opBoolean","COPY",FACE,{"derivedFrom":makeQuery(id+"F3.opExtrude","CAP_FACE",FACE,{"disambiguationData":[OSD([subQ0,subQ1,subQ2,subQ3,subQ4,subQ5,subQ6,subQ7])],"isStart":false})})}),makeQuery(id+"F8.opExtrude","SWEPT_FACE",FACE,{"disambiguationData":[OSD([sQuery(id+"F7.wireOp",EDGE,"E67")])]})]});}
            var Q5;
            Q5=makeQuery(id+"F8.boolean.opBoolean","INTERSECT",EDGE,{"disambiguationData":[OD(0.0)],"derivedFrom":[makeQuery(id+"F5.opExtrude","SWEPT_FACE",FACE,{"disambiguationData":[OSD([sQuery(id+"F4.wireOp",EDGE,"E30")])]}),makeQuery(id+"F8.opExtrude","SWEPT_FACE",FACE,{"disambiguationData":[OSD([sQuery(id+"F7.wireOp",EDGE,"E67")])]})]});
            fillet(context, id + "F14", {"entities" : qUnion([Q0, Q1, Q2, Q3, Q4, Q5]), "radius" : 3 * mm, "tangentPropagation" : true, "allowEdgeOverflow" : false});
        }
        {
            var Q0;
            Q0=makeQuery(id+"F1.opExtrude","CAP_EDGE",EDGE,{"disambiguationData":[OSD([sQuery(id+"F0.wireOp",EDGE,"E1.bottom")])],"isStart":false});
            fillet(context, id + "F15", {"entities" : qUnion([Q0]), "radius" : 2 * mm, "tangentPropagation" : true, "allowEdgeOverflow" : false});
        }
        {
            var Q0;
            {var subQ0=sQuery(id+"F0.wireOp",EDGE,"E22.filletArc");var subQ1=sQuery(id+"F0.wireOp",EDGE,"E7");var subQ2=sQuery(id+"F0.wireOp",EDGE,"E6");var subQ3=sQuery(id+"F0.wireOp",EDGE,"E5");var subQ4=sQuery(id+"F0.wireOp",EDGE,"E4");var subQ5=sQuery(id+"F0.wireOp",EDGE,"E1.bottom");var subQ6=sQuery(id+"F0.wireOp",EDGE,"E21.filletArc");var subQ7=sQuery(id+"F0.wireOp",EDGE,"E1.top");var subQ8=sQuery(id+"F0.wireOp",EDGE,"E1.left");var subQ9=sQuery(id+"F0.wireOp",EDGE,"E1.right");var subQ10=sQuery(id+"F0.wireOp",EDGE,"E23.filletArc");var subQ11=sQuery(id+"F0.wireOp",EDGE,"E24.filletArc");Q0=makeQuery(id+"F2.boolean.opBoolean","SPLIT",FACE,{"disambiguationData":[TD([makeQuery(id+"F1.opExtrude","SWEPT_FACE",FACE,{"disambiguationData":[OSD([subQ5])]})])],"derivedFrom":makeQuery(id+"F1.opExtrude","CAP_FACE",FACE,{"disambiguationData":[OSD([subQ5,subQ7,subQ8,subQ9,subQ4,subQ3,subQ2,subQ1,subQ6,subQ0,subQ10,subQ11])],"isStart":true})});}
            var sketch = newSketch(context, id + "F16", { "sketchPlane" : qUnion([Q0])});
            skCircle(sketch, "E79", {"center": v(0, 120) * mm, "radius": 6 * mm});
            skLineSegment(sketch, "E80", {"start": v(0, 120) * mm, "end": v(0, 90) * mm, "construction": true});
            skArc(sketch, "E81", {"start": v(-15, 120) * mm, "mid": v(0, 135) * mm, "end": v(15, 120) * mm});
            skLineSegment(sketch, "E82", {"start": v(-15, 120) * mm, "end": v(-15, 108) * mm});
            skLineSegment(sketch, "E83", {"start": v(15, 120) * mm, "end": v(15, 108) * mm});
            skLineSegment(sketch, "E84", {"start": v(15, 108) * mm, "end": v(33, 90) * mm});
            skLineSegment(sketch, "E85", {"start": v(-15, 108) * mm, "end": v(-33, 90) * mm});
            skLineSegment(sketch, "E86", {"start": v(-33, 90) * mm, "end": v(33, 90) * mm, "construction": true});
            skLineSegment(sketch, "E87", {"start": v(-80, 0) * mm, "end": v(80, 0) * mm, "construction": true});
            skLineSegment(sketch, "E88.MirrorCS", {"start": v(-15, -120) * mm, "end": v(-15, -108) * mm});
            skLineSegment(sketch, "E89.MirrorCS", {"start": v(15, -120) * mm, "end": v(15, -108) * mm});
            skLineSegment(sketch, "E90.MirrorCS", {"start": v(-15, -108) * mm, "end": v(-33, -90) * mm});
            skLineSegment(sketch, "E91.MirrorCS", {"start": v(-33, -90) * mm, "end": v(33, -90) * mm, "construction": true});
            skArc(sketch, "E92.MirrorCS", {"start": v(-15, -120) * mm, "mid": v(0, -135) * mm, "end": v(15, -120) * mm});
            skLineSegment(sketch, "E93.MirrorCS", {"start": v(15, -108) * mm, "end": v(33, -90) * mm});
            skCircle(sketch, "E94.MirrorC", {"center": v(0, -120) * mm, "radius": 6 * mm});
            skLineSegment(sketch, "E95.MirrorCS", {"start": v(0, -120) * mm, "end": v(0, -90) * mm, "construction": true});
            skSolve(sketch);
        }
        {
            var Q0;
            Q0=makeQuery(id+"F16.imprint","IMPRINT",FACE,{"disambiguationData":[TD([[makeQuery(id+"F16.imprint","IMPRINT",EDGE,{"derivedFrom":makeQuery(id+"F1.opExtrude","CAP_EDGE",EDGE,{"disambiguationData":[OSD([sQuery(id+"F0.wireOp",EDGE,"E1.left")])],"isStart":true})}),-1.0]])]});
            var Q1;
            Q1=makeQuery(id+"F16.imprint","IMPRINT",FACE,{"disambiguationData":[TD([[makeQuery(id+"F16.imprint","IMPRINT",EDGE,{"derivedFrom":sQuery(id+"F16.wireOp",EDGE,"E79")}),-1.0]])]});
            var Q2;
            Q2=makeQuery(id+"F16.imprint","IMPRINT",FACE,{"disambiguationData":[TD([[makeQuery(id+"F16.imprint","IMPRINT",EDGE,{"derivedFrom":sQuery(id+"F16.wireOp",EDGE,"E88.MirrorCS")}),-1.0]])]});
            var Q3;
            Q3=makeQuery(id+"F2.opExtrude","CAP_FACE",FACE,{"disambiguationData":[OSD([sQuery(id+"F0.wireOp",EDGE,"E12"),sQuery(id+"F0.wireOp",EDGE,"E13"),sQuery(id+"F0.wireOp",EDGE,"E14"),sQuery(id+"F0.wireOp",EDGE,"E15"),sQuery(id+"F0.wireOp",EDGE,"E17.filletArc"),sQuery(id+"F0.wireOp",EDGE,"E18.filletArc"),sQuery(id+"F0.wireOp",EDGE,"E19.filletArc"),sQuery(id+"F0.wireOp",EDGE,"E20.filletArc"),sQuery(id+"F0.wireOp",EDGE,"E25.0"),sQuery(id+"F0.wireOp",EDGE,"E25.1"),sQuery(id+"F0.wireOp",EDGE,"E25.2"),sQuery(id+"F0.wireOp",EDGE,"E25.3"),sQuery(id+"F0.wireOp",EDGE,"E25.4"),sQuery(id+"F0.wireOp",EDGE,"E25.5"),sQuery(id+"F0.wireOp",EDGE,"E25.6"),sQuery(id+"F0.wireOp",EDGE,"E25.7")])],"isStart":false});
            extrude(context, id + "F17", {"entities" : qUnion([Q0, Q1, Q2]), "endBound" : BoundingType.UP_TO_SURFACE, "endBoundEntityFace" : qUnion([Q3]), "depth" : 25 * mm});
        }
    });
